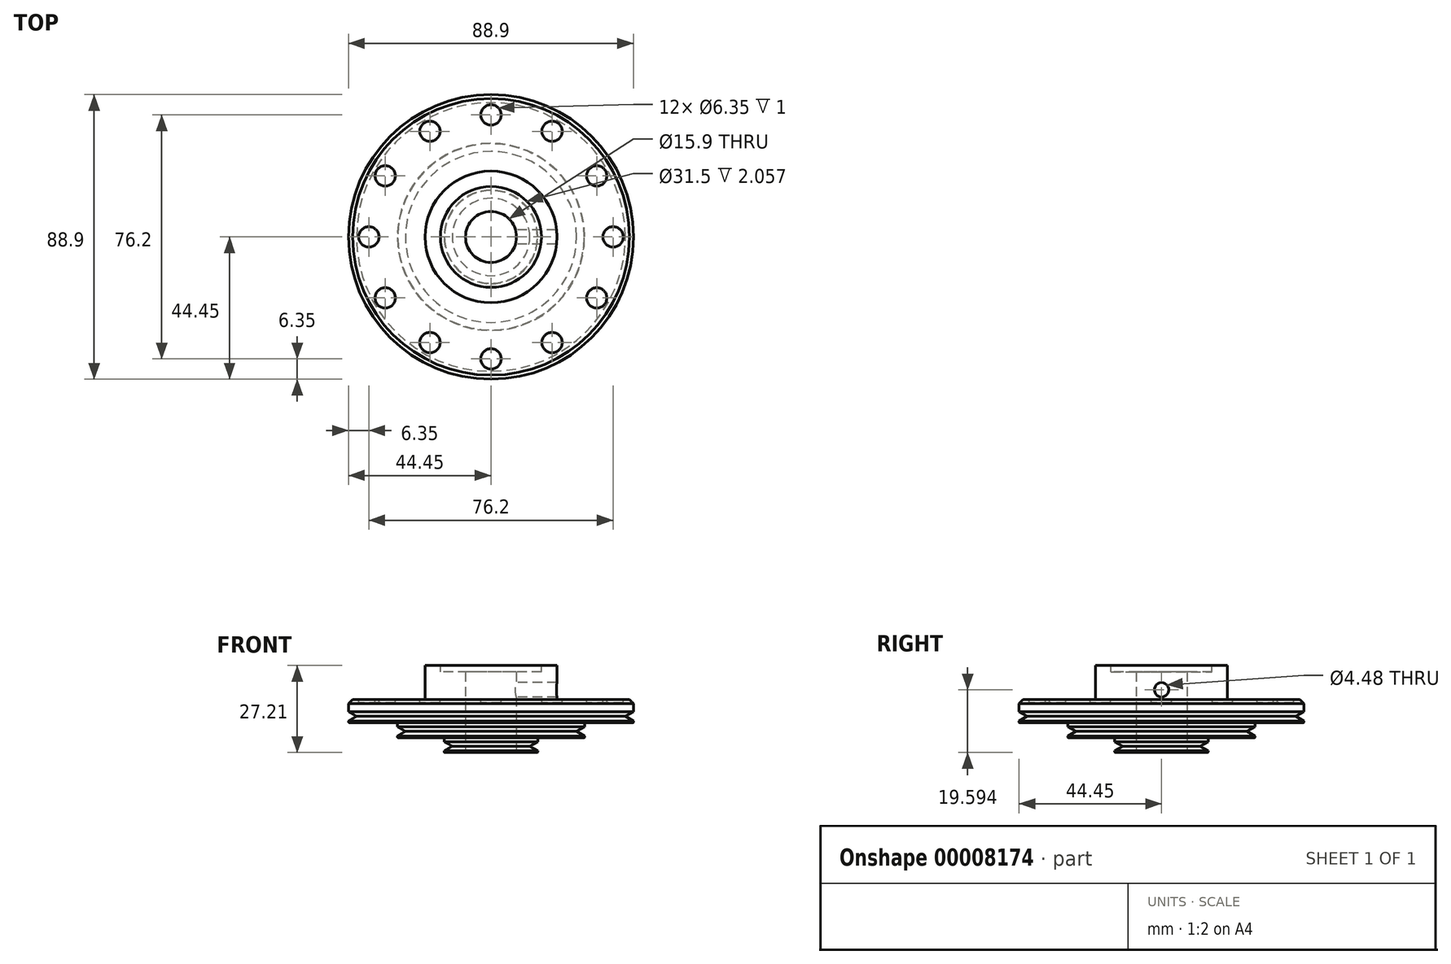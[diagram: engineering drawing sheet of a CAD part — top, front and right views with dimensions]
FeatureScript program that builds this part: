
annotation { "Feature Type Name" : "Feature", "Feature Type Description" : "" }
export const myFeature = defineFeature(function(context is Context, id is Id, definition is map)
    precondition{}
    {
        {
            var Q0;
            Q0=qCreatedBy(makeId("Front.planeOp"),FACE);
            var sketch = newSketch(context, id + "F0", { "sketchPlane" : qUnion([Q0])});
            skLineSegment(sketch, "E0", {"start": v(0, -4.85) * mm, "end": v(0, 37.15) * mm, "construction": true});
            skLineSegment(sketch, "E1", {"start": v(0, 0) * mm, "end": v(-14.6, 0) * mm});
            skLineSegment(sketch, "E2", {"start": v(-14.6, 0) * mm, "end": v(-14.6, 0.5) * mm});
            skLineSegment(sketch, "E3", {"start": v(-14.6, 0.5) * mm, "end": v(-12.1, 1.96) * mm});
            skLineSegment(sketch, "E4", {"start": v(-12.1, 1.96) * mm, "end": v(-14.6, 3.41) * mm});
            skLineSegment(sketch, "E5", {"start": v(-14.6, 3.41) * mm, "end": v(-14.6, 4.68) * mm});
            skLineSegment(sketch, "E6", {"start": v(-14.6, 4.68) * mm, "end": v(-29.21, 4.68) * mm});
            skLineSegment(sketch, "E7", {"start": v(-29.21, 4.68) * mm, "end": v(-29.21, 5.19) * mm});
            skLineSegment(sketch, "E8", {"start": v(-29.2, 5.19) * mm, "end": v(-26.7, 6.64) * mm});
            skLineSegment(sketch, "E9", {"start": v(-26.7, 6.64) * mm, "end": v(-29.2, 8.1) * mm});
            skLineSegment(sketch, "E10", {"start": v(-29.21, 8.1) * mm, "end": v(-29.21, 9.36) * mm});
            skLineSegment(sketch, "E11", {"start": v(-29.21, 9.36) * mm, "end": v(-44.45, 9.36) * mm});
            skLineSegment(sketch, "E12", {"start": v(-44.45, 9.36) * mm, "end": v(-44.45, 9.87) * mm});
            skLineSegment(sketch, "E13", {"start": v(-44.45, 9.87) * mm, "end": v(-41.94, 11.32) * mm});
            skLineSegment(sketch, "E14", {"start": v(-41.94, 11.32) * mm, "end": v(-44.45, 12.77) * mm});
            skLineSegment(sketch, "E15", {"start": v(-44.45, 12.77) * mm, "end": v(-44.45, 16.58) * mm});
            skLineSegment(sketch, "E16", {"start": v(-44.45, 16.58) * mm, "end": v(-20.57, 16.58) * mm});
            skLineSegment(sketch, "E17", {"start": v(-20.57, 16.58) * mm, "end": v(-20.57, 27.21) * mm});
            skLineSegment(sketch, "E18", {"start": v(-20.57, 27.21) * mm, "end": v(0, 27.21) * mm});
            skLineSegment(sketch, "E19", {"start": v(0, 0) * mm, "end": v(0, 27.21) * mm});
            skSolve(sketch);
        }
        {
            var Q0;
            Q0 = qSketchRegion(id + "F0", true);
            var Q1;
            Q1=sQuery(id+"F0.wireOp",EDGE,"E0");
            revolve(context, id + "F1", {"entities" : qUnion([Q0]), "axis" : qUnion([Q1]), "revolveType" : RevolveType.FULL});
        }
        {
            var Q0;
            Q0=qCreatedBy(makeId("Top.planeOp"),FACE);
            var sketch = newSketch(context, id + "F2", { "sketchPlane" : qUnion([Q0])});
            skCircle(sketch, "E20", {"center": v(0, 0) * mm, "radius": 7.95 * mm});
            skSolve(sketch);
        }
        {
            var Q0;
            Q0 = qSketchRegion(id + "F2", true);
            var Q1;
            Q1=makeQuery(id+"F1.opRevolve","SWEPT_FACE",FACE,{"disambiguationData":[OSD([sQuery(id+"F0.wireOp",EDGE,"E18")])]});
            extrude(context, id + "F3", {"entities" : qUnion([Q0]), "operationType" : NewBodyOperationType.REMOVE, "endBound" : BoundingType.UP_TO_SURFACE, "endBoundEntityFace" : qUnion([Q1]), "depth" : 25.4 * mm});
        }
        {
            var Q0;
            Q0=qCreatedBy(makeId("Right.planeOp"),FACE);
            var sketch = newSketch(context, id + "F4", { "sketchPlane" : qUnion([Q0])});
            skLineSegment(sketch, "E21", {"start": v(0, 0) * mm, "end": v(0, 9.47) * mm, "construction": true});
            skCircle(sketch, "E22", {"center": v(0, 19.6) * mm, "radius": 2.24 * mm});
            skSolve(sketch);
        }
        {
            var Q0;
            Q0 = qSketchRegion(id + "F4", true);
            extrude(context, id + "F5", {"entities" : qUnion([Q0]), "operationType" : NewBodyOperationType.REMOVE, "depth" : 25.4 * mm});
        }
        {
            var Q0;
            Q0=makeQuery(id+"F1.opRevolve","SWEPT_FACE",FACE,{"disambiguationData":[OSD([sQuery(id+"F0.wireOp",EDGE,"E18")])]});
            var sketch = newSketch(context, id + "F6", { "sketchPlane" : qUnion([Q0])});
            skCircle(sketch, "E23", {"center": v(0, 0) * mm, "radius": 15.75 * mm});
            skSolve(sketch);
        }
        {
            var Q0;
            Q0 = qSketchRegion(id + "F6", true);
            extrude(context, id + "F7", {"entities" : qUnion([Q0]), "operationType" : NewBodyOperationType.REMOVE, "oppositeDirection" : true, "depth" : 2.06 * mm});
        }
        {
            var Q0;
            Q0=makeQuery(id+"F1.opRevolve","SWEPT_FACE",FACE,{"disambiguationData":[OSD([sQuery(id+"F0.wireOp",EDGE,"E16")])]});
            var sketch = newSketch(context, id + "F8", { "sketchPlane" : qUnion([Q0])});
            skCircle(sketch, "E24", {"center": v(0, 38.1) * mm, "radius": 3.18 * mm});
            skCircle(sketch, "E25.1.0", {"center": v(-19.05, 33) * mm, "radius": 3.18 * mm});
            skCircle(sketch, "E25.2.0", {"center": v(-33, 19.05) * mm, "radius": 3.18 * mm});
            skCircle(sketch, "E25.3.0", {"center": v(-38.1, 0) * mm, "radius": 3.18 * mm});
            skCircle(sketch, "E25.4.0", {"center": v(-33, -19.05) * mm, "radius": 3.18 * mm});
            skCircle(sketch, "E25.5.0", {"center": v(-19.05, -33) * mm, "radius": 3.18 * mm});
            skCircle(sketch, "E25.6.0", {"center": v(0, -38.1) * mm, "radius": 3.18 * mm});
            skCircle(sketch, "E25.7.0", {"center": v(19.05, -33) * mm, "radius": 3.18 * mm});
            skCircle(sketch, "E25.8.0", {"center": v(33, -19.05) * mm, "radius": 3.18 * mm});
            skCircle(sketch, "E25.9.0", {"center": v(38.1, 0) * mm, "radius": 3.18 * mm});
            skCircle(sketch, "E25.10.0", {"center": v(33, 19.05) * mm, "radius": 3.18 * mm});
            skCircle(sketch, "E25.11.0", {"center": v(19.05, 33) * mm, "radius": 3.18 * mm});
            skPoint(sketch, "E25.center", {"position": v(0, 0) * mm});
            skSolve(sketch);
        }
        {
            var Q0;
            Q0 = qSketchRegion(id + "F8", true);
            extrude(context, id + "F9", {"entities" : qUnion([Q0]), "operationType" : NewBodyOperationType.REMOVE, "oppositeDirection" : true, "depth" : 1 * mm});
        }
        {
            var Q0;
            Q0=makeQuery(id+"F1.opRevolve","SWEPT_EDGE",EDGE,{"disambiguationData":[OSD([sQuery(id+"F0.wireOp",EDGE,"E1"),sQuery(id+"F0.wireOp",EDGE,"E2")])]});
            var Q1;
            Q1=makeQuery(id+"F1.opRevolve","SWEPT_EDGE",EDGE,{"disambiguationData":[OSD([sQuery(id+"F0.wireOp",EDGE,"E6"),sQuery(id+"F0.wireOp",EDGE,"E7")])]});
            var Q2;
            Q2=makeQuery(id+"F1.opRevolve","SWEPT_EDGE",EDGE,{"disambiguationData":[OSD([sQuery(id+"F0.wireOp",EDGE,"E11"),sQuery(id+"F0.wireOp",EDGE,"E12")])]});
            chamfer(context, id + "F10", {"entities" : qUnion([Q0, Q1, Q2]), "width" : 0.13 * mm, "tangentPropagation" : true});
        }
        {
            var Q0;
            Q0=makeQuery(id+"F1.opRevolve","SWEPT_EDGE",EDGE,{"disambiguationData":[OSD([sQuery(id+"F0.wireOp",EDGE,"E15"),sQuery(id+"F0.wireOp",EDGE,"E16")])]});
            chamfer(context, id + "F11", {"entities" : qUnion([Q0]), "width" : 1.27 * mm, "tangentPropagation" : true});
        }
    });
